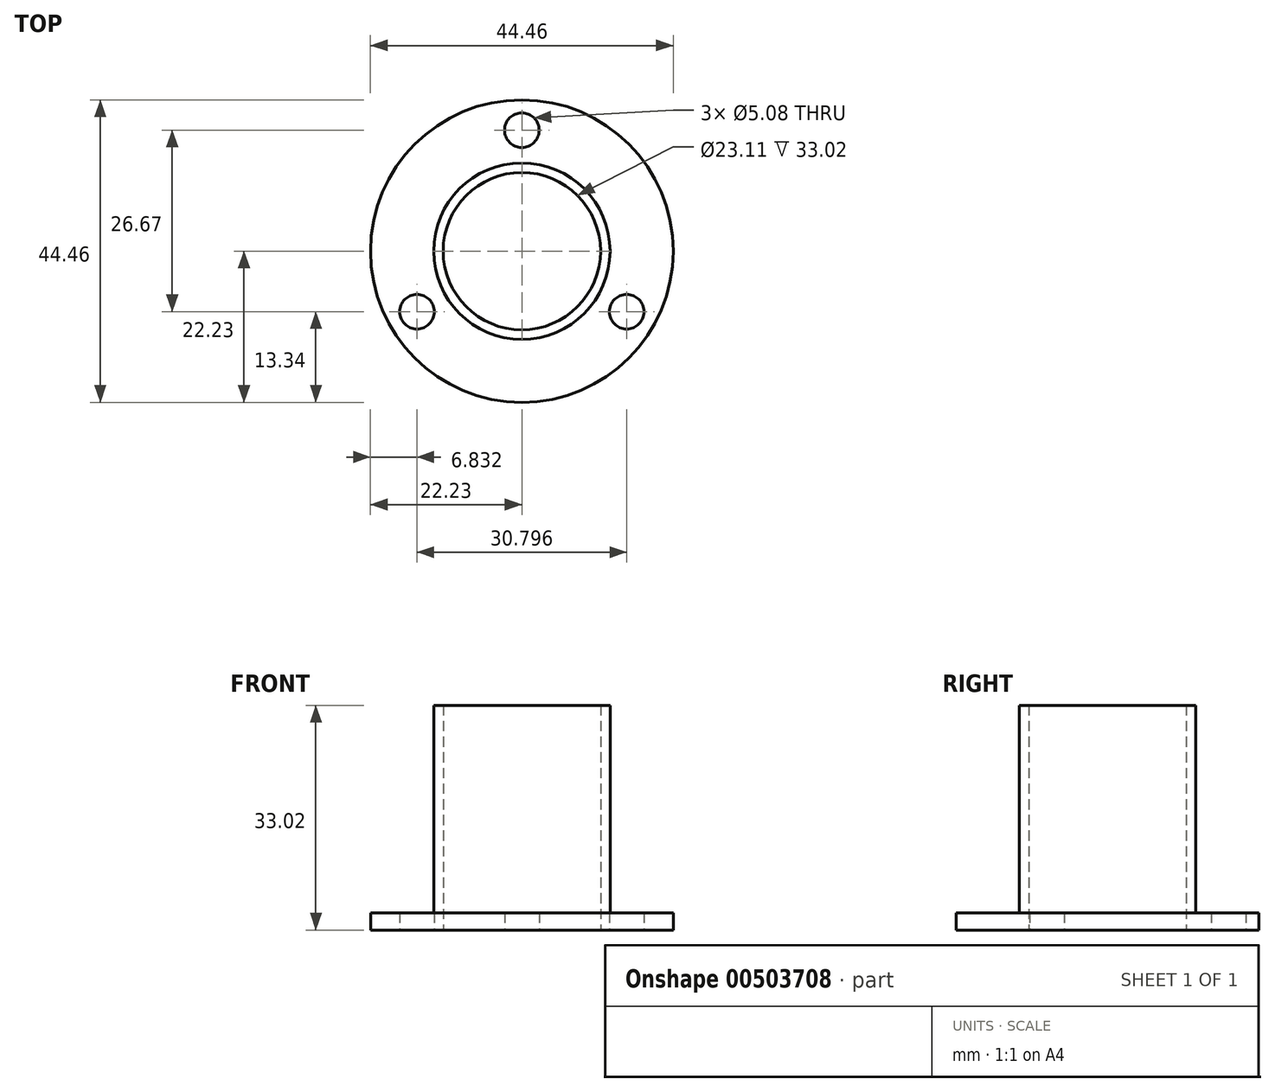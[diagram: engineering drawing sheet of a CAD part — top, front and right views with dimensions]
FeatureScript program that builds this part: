
annotation { "Feature Type Name" : "Feature", "Feature Type Description" : "" }
export const myFeature = defineFeature(function(context is Context, id is Id, definition is map)
    precondition{}
    {
        {
            var Q0;
            Q0=qCreatedBy(makeId("Top.planeOp"),FACE);
            var sketch = newSketch(context, id + "F0", { "sketchPlane" : qUnion([Q0])});
            skCircle(sketch, "E0", {"center": v(0, 0) * mm, "radius": 12.95 * mm});
            skCircle(sketch, "E1", {"center": v(0, 0) * mm, "radius": 22.23 * mm});
            skCircle(sketch, "E2", {"center": v(0, 17.78) * mm, "radius": 2.54 * mm});
            skCircle(sketch, "E3", {"center": v(15.4, -8.9) * mm, "radius": 2.54 * mm});
            skCircle(sketch, "E4", {"center": v(-15.4, -8.9) * mm, "radius": 2.54 * mm});
            skCircle(sketch, "E5", {"center": v(0, 0) * mm, "radius": 11.56 * mm});
            skSolve(sketch);
        }
        {
            var Q0;
            Q0=makeQuery(id+"F0.imprint","IMPRINT",FACE,{"disambiguationData":[TD([[makeQuery(id+"F0.imprint","IMPRINT",EDGE,{"derivedFrom":sQuery(id+"F0.wireOp",EDGE,"E0")}),1.0]])]});
            extrude(context, id + "F1", {"entities" : qUnion([Q0]), "depth" : 33.02 * mm});
        }
        {
            var Q0;
            Q0=qSketchRegion(id+"F0",true);
            extrude(context, id + "F2", {"entities" : qUnion([Q0]), "operationType" : NewBodyOperationType.ADD, "depth" : 2.54 * mm});
        }
    });
